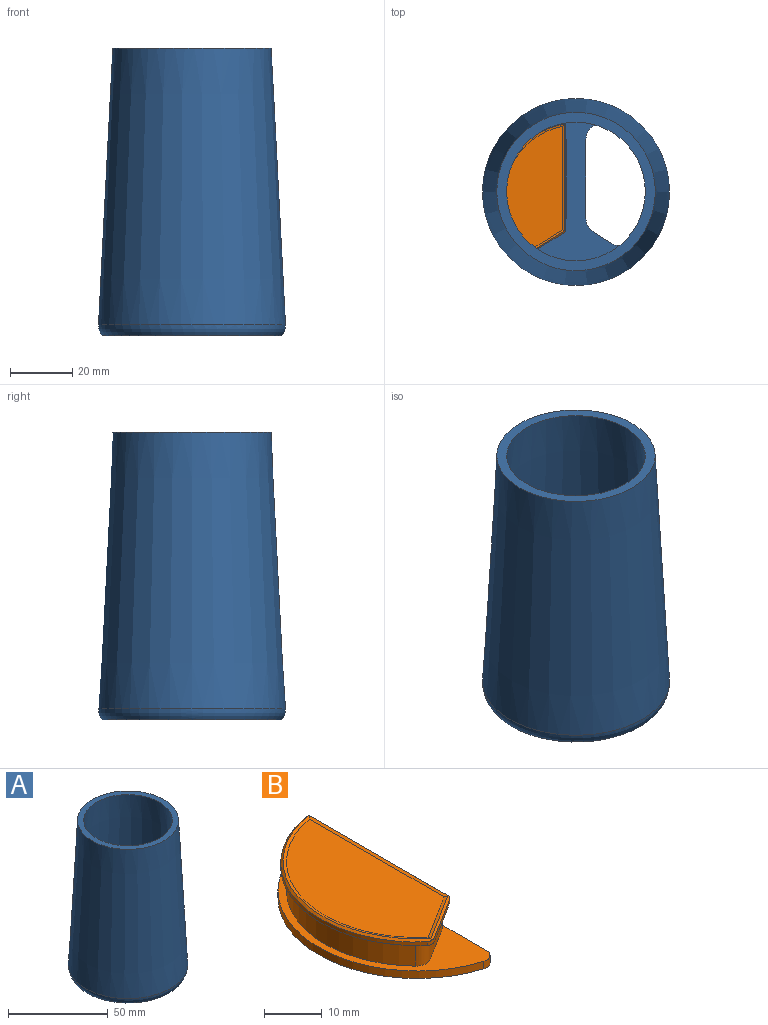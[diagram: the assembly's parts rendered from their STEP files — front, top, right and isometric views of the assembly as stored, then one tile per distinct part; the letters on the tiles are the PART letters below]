
ASSEMBLY  parts=2 mates=1
PART A: 20 faces, bbox 64.9x64.9x92.4 mm
  f0: plane 56.27x56.27mm, normal (0,0,1), area 1198mm2, adj f4,f6,f7,f8,f9,f10,f11,f12
  f1: plane 54.84x54.84mm, normal (0,0,-1), area 1073.2mm2, adj f5,f6,f7,f8,f9,f10,f11,f12
  f2: plane 50.8x50.8mm, normal (0,0,1), area 475mm2, adj f3,f4
  f3: cone r=25.4mm half-angle=3deg, axis (0,0,-1), area 15431.9mm2, adj f2,f19
  f4: cone r=22.23mm half-angle=3.9deg, axis (0,0,-1), area 13595.4mm2, adj f0,f2
  f5: cone r=22.86mm half-angle=3deg, axis (0,0,-1), area 450.6mm2, adj f1,f18
  f6: cylinder r=23.81mm len=36.91mm, axis (0,0,-1), area 110.4mm2, adj f0,f1,f12,f14
  f7: plane 25.32x2.54mm, normal (1,0,0), area 64.3mm2, adj f0,f1,f12,f13
  f8: plane 5.95x3.71mm, normal (0.53,0.85,0), area 17.8mm2, adj f0,f1,f13,f14
  f9: plane 25.32x2.54mm, normal (-1,0,0), area 64.3mm2, adj f0,f1,f15,f17
  f10: cylinder r=23.81mm len=36.91mm, axis (0,0,-1), area 110.4mm2, adj f0,f1,f16,f17
  f11: plane 5.95x3.71mm, normal (-0.53,0.85,0), area 17.8mm2, adj f0,f1,f15,f16
  f12: cylinder r=5.08mm len=7.32mm, axis (0,0,-1), area 26.2mm2, adj f0,f1,f6,f7
  f13: cylinder r=5.08mm len=4.31mm, axis (0,0,1), area 13.1mm2, adj f0,f1,f7,f8
  f14: cylinder r=5.08mm len=6.54mm, axis (0,0,-1), area 18.3mm2, adj f0,f1,f6,f8
  f15: cylinder r=5.08mm len=4.31mm, axis (0,0,1), area 13.1mm2, adj f0,f1,f9,f11
  f16: cylinder r=5.08mm len=6.54mm, axis (0,0,-1), area 18.3mm2, adj f0,f1,f10,f11
  f17: cylinder r=5.08mm len=7.32mm, axis (0,0,-1), area 26.2mm2, adj f0,f1,f9,f10
  f18: torus R=28.83mm, axis (0,0,-1), area 339.8mm2, adj f5,f19
  f19: torus R=24.91mm, axis (0,0,-1), area 701.6mm2, adj f3,f18
PART B: 52 faces, bbox 23.3x49.4x8.5 mm
  f0: plane 46.68x19.95mm, normal (0,0,-1), area 310.4mm2, adj f8,f16,f23,f24,f25,f26,f27,f28
  f1: plane 41.69x20.64mm, normal (0,0,-1), area 110.5mm2, adj f2,f3,f4,f6,f7,f8,f17,f18
  f2: plane 32.72x0.76mm, normal (1,0,0), area 24.9mm2, adj f1,f9,f17,f19
  f3: cylinder r=23.81mm len=41.35mm, axis (0,0,-1), area 40.5mm2, adj f1,f10,f17,f18
  f4: plane 10.3x6.43mm, normal (0.53,-0.85,0), area 9.3mm2, adj f1,f11,f18,f19
  f5: plane 39.77x18.61mm, normal (0,0,1), area 558.7mm2, adj f12,f13,f14
  f6: plane 7.69x5.08mm, normal (0.53,-0.85,0), area 46.1mm2, adj f1,f15,f20,f22
  f7: cylinder r=22.8mm len=37.32mm, axis (0,0,1), area 231.1mm2, adj f1,f15,f20,f21
  f8: plane 42.61x6.67mm, normal (1,0,0), area 211.7mm2, adj f0,f1,f15,f21,f22,f23,f24
  f9: plane 34.27x0.41mm, normal (0.71,0,0.71), area 19.7mm2, adj f2,f11,f12,f17,f19
  f10: cone r=23.3mm half-angle=45deg, axis (0,0,-1), area 31.4mm2, adj f3,f11,f13,f17,f18
  f11: plane 11.5x7.22mm, normal (0.37,-0.6,0.71), area 7.7mm2, adj f4,f9,f10,f14,f18,f19
  f12: cylinder r=5.08mm len=34.17mm, axis (0,-1,0), area 21mm2, adj f5,f9,f13,f14,f17
  f13: torus R=24.38mm, axis (0,0,1), area 32.8mm2, adj f5,f10,f12,f14,f17
  f14: cylinder r=5.08mm len=11.56mm, axis (-0.85,-0.53,0), area 8mm2, adj f5,f11,f12,f13
  f15: plane 46.68x19.95mm, normal (0,0,1), area 163.8mm2, adj f6,f7,f8,f16,f20,f21,f22,f23
  f16: cylinder r=24.26mm len=46.51mm, axis (0,0,1), area 98.7mm2, adj f0,f15,f23,f24
  f17: cylinder r=1.27mm len=1.52mm, axis (0,0,-1), area 2.1mm2, adj f1,f2,f3,f9,f10,f12,f13
  f18: cylinder r=1.27mm len=1.5mm, axis (0,0,-1), area 1.4mm2, adj f1,f3,f4,f10,f11
  f19: cylinder r=1.27mm len=1.08mm, axis (0,0,-1), area 1mm2, adj f1,f2,f4,f9,f11
  f20: cylinder r=2.54mm len=5.08mm, axis (0,0,1), area 17.5mm2, adj f1,f6,f7,f15
  f21: cylinder r=2.54mm len=5.08mm, axis (0,0,1), area 24.7mm2, adj f1,f7,f8,f15
  f22: cylinder r=2.54mm len=5.08mm, axis (0,0,1), area 13.1mm2, adj f1,f6,f8,f15
  f23: cylinder r=2.03mm len=2.61mm, axis (0,0,1), area 6mm2, adj f0,f8,f15,f16
  f24: cylinder r=2.03mm len=2.61mm, axis (0,0,1), area 6mm2, adj f0,f8,f15,f16
  f25: cylinder r=0.76mm len=1.02mm, axis (0,0,1), area 1.2mm2, adj f0,f26,f30,f31
  f26: plane 28.37x0.83mm, normal (-1,0,0), area 23.4mm2, adj f0,f25,f27,f31
  f27: cylinder r=0.76mm len=0.83mm, axis (0,0,1), area 0.6mm2, adj f0,f26,f28,f31
  f28: plane 7.69x4.8mm, normal (-0.53,0.85,0), area 7.5mm2, adj f0,f27,f29,f31
  f29: cylinder r=0.76mm len=0.95mm, axis (0,0,1), area 0.9mm2, adj f0,f28,f30,f31
  f30: cylinder r=21.02mm len=34.41mm, axis (0,0,1), area 34.6mm2, adj f0,f25,f29,f31
  f31: plane 34.69x14.93mm, normal (0,0,-1), area 392.8mm2, adj f25,f26,f27,f28,f29,f30
  f32: plane 6.64x4.15mm, normal (-0.53,0.85,0), area 2mm2, adj f0,f33,f35,f51
  f33: plane 0.6x0.51mm, normal (1,0,0), area 0.3mm2, adj f0,f32,f34,f51
  f34: plane 6.24x3.89mm, normal (0.53,-0.85,0), area 1.9mm2, adj f0,f33,f35,f51
  f35: plane 0.54x0.44mm, normal (-0.64,-0.77,0), area 0.2mm2, adj f0,f32,f34,f51
  f36: plane 5.21x3.25mm, normal (-0.53,0.85,0), area 1.6mm2, adj f0,f37,f39,f50
  f37: plane 0.6x0.51mm, normal (1,0,0), area 0.3mm2, adj f0,f36,f38,f50
  f38: plane 4.81x3mm, normal (0.53,-0.85,0), area 1.4mm2, adj f0,f37,f39,f50
  f39: plane 0.54x0.44mm, normal (-0.64,-0.77,0), area 0.2mm2, adj f0,f36,f38,f50
  f40: plane 3.78x2.36mm, normal (-0.53,0.85,0), area 1.1mm2, adj f0,f41,f43,f49
  f41: plane 0.6x0.51mm, normal (1,0,0), area 0.3mm2, adj f0,f40,f42,f49
  f42: plane 3.38x2.11mm, normal (0.53,-0.85,0), area 1mm2, adj f0,f41,f43,f49
  f43: plane 0.54x0.44mm, normal (-0.64,-0.77,0), area 0.2mm2, adj f0,f40,f42,f49
  f44: plane 2.35x1.47mm, normal (-0.53,0.85,0), area 0.7mm2, adj f0,f45,f47,f48
  f45: plane 0.6x0.51mm, normal (1,0,0), area 0.3mm2, adj f0,f44,f46,f48
  f46: plane 1.94x1.21mm, normal (0.53,-0.85,0), area 0.6mm2, adj f0,f45,f47,f48
  f47: plane 0.54x0.44mm, normal (-0.64,-0.77,0), area 0.2mm2, adj f0,f44,f46,f48
  f48: cylinder r=0.25mm len=2.62mm, axis (-0.85,-0.53,0), area 2mm2, adj f44,f45,f46,f47
  f49: cylinder r=0.25mm len=4.05mm, axis (-0.85,-0.53,0), area 3.4mm2, adj f40,f41,f42,f43
  f50: cylinder r=0.25mm len=5.48mm, axis (-0.85,-0.53,0), area 4.7mm2, adj f36,f37,f38,f39
  f51: cylinder r=0.25mm len=6.91mm, axis (-0.85,-0.53,0), area 6.1mm2, adj f32,f33,f34,f35
PLACE A t=(-33.28,-6.71,-45.49)mm
PLACE B t=(-33.34,-8.07,-36.6)mm
MATE fastened A.f1 <-> B.f15  axis (0,0,-1) through (-38.85,-19.53,-41.68)mm
